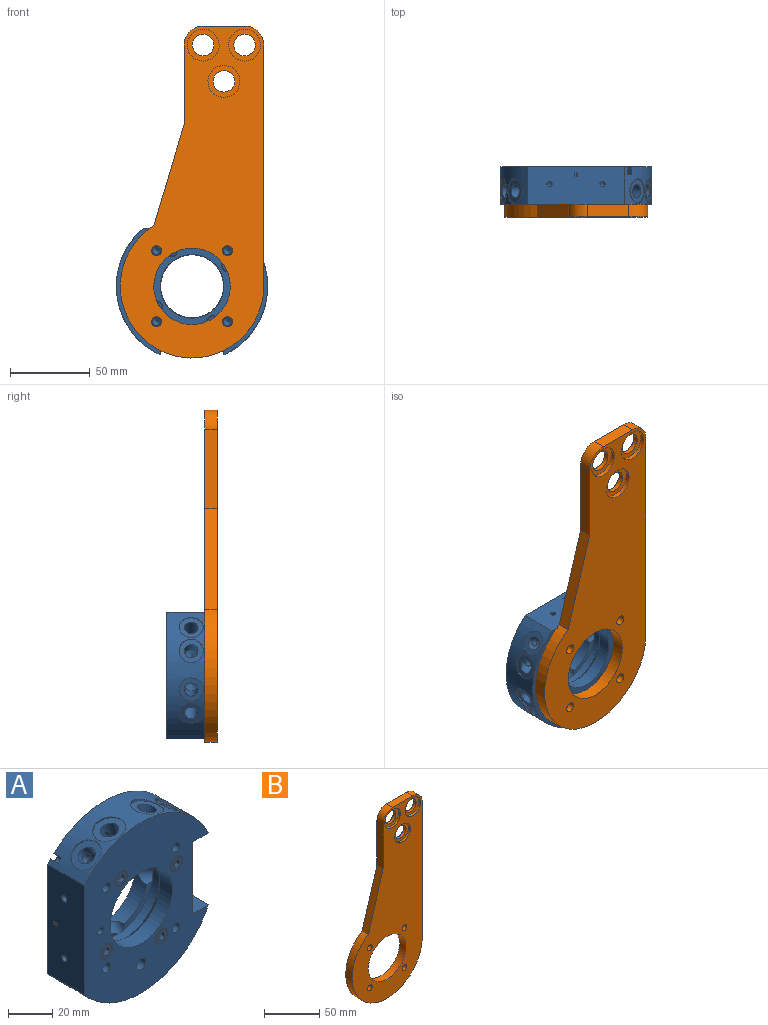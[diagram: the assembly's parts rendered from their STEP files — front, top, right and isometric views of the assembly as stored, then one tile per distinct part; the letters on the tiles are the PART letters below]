
ASSEMBLY  parts=2 mates=1
PART A: 247 faces, bbox 80.7x25x96.8 mm
  f0: plane 0.1x0.04mm, normal (0,0,-1), area 0mm2, adj f207,f224,f225,f241
  f1: plane 0.1x0.04mm, normal (0,0,1), area 0mm2, adj f207,f226,f227,f241
  f2: plane 0.5x0.1mm, normal (0,-0.89,-0.45), area 0.1mm2, adj f3,f4,f99,f178
  f3: plane 0.5x0.1mm, normal (0,0.89,-0.45), area 0.1mm2, adj f2,f5,f99,f178
  f4: plane 0.5x0.21mm, normal (0,-0.59,-0.8), area 0.1mm2, adj f2,f6,f99,f178
  f5: plane 0.5x0.21mm, normal (0,0.59,-0.8), area 0.1mm2, adj f3,f9,f99,f178
  f6: plane 0.5x0.16mm, normal (0,-0.31,-0.95), area 0.1mm2, adj f4,f14,f99,f178
  f7: plane 0.5x0.11mm, normal (0,0,1), area 0.1mm2, adj f15,f16,f56,f99
  f8: plane 0.5x0.16mm, normal (0,0,1), area 0.1mm2, adj f17,f18,f59,f99
  f9: plane 0.5x0.16mm, normal (0,0.31,-0.95), area 0.1mm2, adj f5,f19,f99,f178
  f10: plane 4.62x4mm, normal (0,-1,0), area 13.9mm2, adj f20,f21,f22,f23,f24,f25
  f11: plane 4.62x4mm, normal (0,-1,0), area 13.9mm2, adj f26,f27,f28,f29,f30,f31
  f12: plane 4.62x4mm, normal (0,-1,0), area 13.9mm2, adj f32,f33,f34,f35,f36,f37
  f13: plane 4.62x4mm, normal (0,-1,0), area 13.9mm2, adj f38,f39,f40,f41,f42,f43
  f14: plane 0.5x0.21mm, normal (0,0,-1), area 0.1mm2, adj f6,f44,f99,f178
  f15: plane 0.5x0.16mm, normal (0,-0.31,0.95), area 0.1mm2, adj f7,f45,f56,f99
  f16: plane 0.5x0.16mm, normal (0,0.31,0.95), area 0.1mm2, adj f7,f46,f56,f99
  f17: plane 0.5x0.16mm, normal (0,-0.31,0.95), area 0.1mm2, adj f8,f47,f59,f99
  f18: plane 0.5x0.16mm, normal (0,0.31,0.95), area 0.1mm2, adj f8,f48,f59,f99
  f19: plane 0.5x0.27mm, normal (0,0,-1), area 0.1mm2, adj f9,f49,f99,f178
  f20: plane 2x2mm, normal (0.5,0,-0.87), area 4.6mm2, adj f10,f21,f25,f50
  f21: plane 2x2mm, normal (-0.5,0,-0.87), area 4.6mm2, adj f10,f20,f22,f50
  f22: plane 2.31x2mm, normal (-1,0,0), area 4.6mm2, adj f10,f21,f23,f50
  f23: plane 2x2mm, normal (-0.5,0,0.87), area 4.6mm2, adj f10,f22,f24,f50
  f24: plane 2x2mm, normal (0.5,0,0.87), area 4.6mm2, adj f10,f23,f25,f50
  f25: plane 2.31x2mm, normal (1,0,0), area 4.6mm2, adj f10,f20,f24,f50
  f26: plane 2x2mm, normal (0.5,0,-0.87), area 4.6mm2, adj f11,f27,f31,f51
  f27: plane 2x2mm, normal (-0.5,0,-0.87), area 4.6mm2, adj f11,f26,f28,f51
  f28: plane 2.31x2mm, normal (-1,0,0), area 4.6mm2, adj f11,f27,f29,f51
  f29: plane 2x2mm, normal (-0.5,0,0.87), area 4.6mm2, adj f11,f28,f30,f51
  f30: plane 2x2mm, normal (0.5,0,0.87), area 4.6mm2, adj f11,f29,f31,f51
  f31: plane 2.31x2mm, normal (1,0,0), area 4.6mm2, adj f11,f26,f30,f51
  f32: plane 2x2mm, normal (0.5,0,-0.87), area 4.6mm2, adj f12,f33,f37,f52
  f33: plane 2x2mm, normal (-0.5,0,-0.87), area 4.6mm2, adj f12,f32,f34,f52
  f34: plane 2.31x2mm, normal (-1,0,0), area 4.6mm2, adj f12,f33,f35,f52
  f35: plane 2x2mm, normal (-0.5,0,0.87), area 4.6mm2, adj f12,f34,f36,f52
  f36: plane 2x2mm, normal (0.5,0,0.87), area 4.6mm2, adj f12,f35,f37,f52
  f37: plane 2.31x2mm, normal (1,0,0), area 4.6mm2, adj f12,f32,f36,f52
  f38: plane 2x2mm, normal (0.5,0,-0.87), area 4.6mm2, adj f13,f39,f43,f53
  f39: plane 2x2mm, normal (-0.5,0,-0.87), area 4.6mm2, adj f13,f38,f40,f53
  f40: plane 2.31x2mm, normal (-1,0,0), area 4.6mm2, adj f13,f39,f41,f53
  f41: plane 2x2mm, normal (-0.5,0,0.87), area 4.6mm2, adj f13,f40,f42,f53
  f42: plane 2x2mm, normal (0.5,0,0.87), area 4.6mm2, adj f13,f41,f43,f53
  f43: plane 2.31x2mm, normal (1,0,0), area 4.6mm2, adj f13,f38,f42,f53
  f44: plane 0.5x0.16mm, normal (0,0.31,-0.95), area 0.1mm2, adj f14,f54,f99,f178
  f45: plane 0.5x0.11mm, normal (0,-0.7,0.71), area 0.1mm2, adj f15,f55,f56,f99
  f46: plane 0.5x0.11mm, normal (0,0.7,0.71), area 0.1mm2, adj f16,f56,f57,f99
  f47: plane 0.5x0.11mm, normal (0,-0.7,0.71), area 0.1mm2, adj f17,f58,f59,f99
  f48: plane 0.5x0.11mm, normal (0,0.7,0.71), area 0.1mm2, adj f18,f59,f60,f99
  f49: plane 0.5x0.16mm, normal (0,-0.31,-0.95), area 0.1mm2, adj f19,f61,f99,f178
  f50: plane 7x7mm, normal (0,-1,0), area 24.6mm2, adj f20,f21,f22,f23,f24,f25,f63
  f51: plane 7x7mm, normal (0,-1,0), area 24.6mm2, adj f26,f27,f28,f29,f30,f31,f64
  f52: plane 7x7mm, normal (0,-1,0), area 24.6mm2, adj f32,f33,f34,f35,f36,f37,f65
  f53: plane 7x7mm, normal (0,-1,0), area 24.6mm2, adj f38,f39,f40,f41,f42,f43,f66
  f54: plane 0.5x0.21mm, normal (0,0.59,-0.8), area 0.1mm2, adj f44,f67,f99,f178
  f55: plane 0.5x0.16mm, normal (0,-0.95,0.32), area 0.1mm2, adj f45,f56,f68,f99
  f56: plane 1.3x0.74mm, normal (-1,0,0), area 0.9mm2, adj f7,f15,f16,f45,f46,f55,f57,f68
  f57: plane 0.5x0.16mm, normal (0,0.95,0.32), area 0.1mm2, adj f46,f56,f70,f99
  f58: plane 0.5x0.16mm, normal (0,-0.94,0.33), area 0.1mm2, adj f47,f59,f71,f99
  f59: plane 1.3x0.8mm, normal (-1,0,0), area 1mm2, adj f8,f17,f18,f47,f48,f58,f60,f71
  f60: plane 0.5x0.16mm, normal (0,0.95,0.32), area 0.1mm2, adj f48,f59,f73,f99
  f61: plane 0.5x0.21mm, normal (0,-0.59,-0.8), area 0.1mm2, adj f49,f74,f99,f178
  f62: plane 1.44x0.94mm, normal (1,0,0), area 0.7mm2, adj f75,f76,f77
  f63: cylinder r=3.5mm len=7mm, axis (0,1,0), area 127.5mm2, adj f50,f84
  f64: cylinder r=3.5mm len=7mm, axis (0,1,0), area 127.5mm2, adj f51,f85
  f65: cylinder r=3.5mm len=7mm, axis (0,1,0), area 127.5mm2, adj f52,f86
  f66: cylinder r=3.5mm len=7mm, axis (0,1,0), area 127.5mm2, adj f53,f87
  f67: plane 0.5x0.21mm, normal (0,0.79,-0.61), area 0.1mm2, adj f54,f98,f99,f178
  f68: plane 0.99x0.5mm, normal (0,-1,0), area 0.5mm2, adj f55,f56,f69,f99
  f69: plane 0.74x0.5mm, normal (0,0,-1), area 0.4mm2, adj f56,f68,f70,f99
  f70: plane 0.99x0.5mm, normal (0,1,0), area 0.5mm2, adj f56,f57,f69,f99
  f71: plane 0.99x0.5mm, normal (0,-1,0), area 0.5mm2, adj f58,f59,f72,f99
  f72: plane 0.8x0.5mm, normal (0,0,-1), area 0.4mm2, adj f59,f71,f73,f99
  f73: plane 0.99x0.5mm, normal (0,1,0), area 0.5mm2, adj f59,f60,f72,f99
  f74: plane 0.5x0.21mm, normal (0,-0.79,-0.61), area 0.1mm2, adj f61,f99,f100,f178
  f75: plane 1.44x0.5mm, normal (0,0.31,0.95), area 0.8mm2, adj f62,f76,f77,f105
  f76: plane 1.44x0.5mm, normal (0,0.31,-0.95), area 0.8mm2, adj f62,f75,f77,f105
  f77: plane 0.94x0.5mm, normal (0,-1,0), area 0.5mm2, adj f62,f75,f76,f105
  f78: cone r=0mm half-angle=59deg, axis (0,-1,0), area 22.2mm2, adj f112
  f79: cone r=0mm half-angle=59deg, axis (0,-1,0), area 22.2mm2, adj f113
  f80: cone r=0mm half-angle=59deg, axis (0,-1,0), area 22.2mm2, adj f114
  f81: cone r=0mm half-angle=59deg, axis (0,-1,0), area 22.2mm2, adj f115
  f82: plane 4x4mm, normal (0,-1,0), area 12.6mm2, adj f116
  f83: cone r=0mm half-angle=60deg, axis (0,-1,0), area 32.6mm2, adj f117
  f84: plane 8x8mm, normal (0,-1,0), area 11.8mm2, adj f63,f118
  f85: plane 8x8mm, normal (0,-1,0), area 11.8mm2, adj f64,f119
  f86: plane 8x8mm, normal (0,-1,0), area 11.8mm2, adj f65,f120
  f87: plane 8x8mm, normal (0,-1,0), area 11.8mm2, adj f66,f121
  f88: cone r=0mm half-angle=60deg, axis (-0.57,0,-0.82), area 66.5mm2, adj f124
  f89: cone r=0mm half-angle=60deg, axis (0.57,0,-0.82), area 66.5mm2, adj f125
  f90: cone r=0mm half-angle=60deg, axis (0.26,0,-0.97), area 66.5mm2, adj f126
  f91: cone r=0mm half-angle=60deg, axis (-0.26,0,-0.97), area 66.5mm2, adj f127
  f92: cone r=0mm half-angle=60deg, axis (0.57,0,0.82), area 66.5mm2, adj f128
  f93: cone r=0mm half-angle=60deg, axis (-0.57,0,0.82), area 66.5mm2, adj f129
  f94: cone r=0mm half-angle=60deg, axis (-0.26,0,0.97), area 66.5mm2, adj f130
  f95: cone r=0mm half-angle=60deg, axis (0.26,0,0.97), area 66.5mm2, adj f131
  f96: cone r=0mm half-angle=59deg, axis (-1,0,0), area 9.6mm2, adj f137
  f97: cone r=0mm half-angle=59deg, axis (-1,0,0), area 9.6mm2, adj f138
  f98: plane 0.5x0.26mm, normal (0,0.98,-0.2), area 0.1mm2, adj f67,f99,f139,f178
  f99: plane 2.5x1.93mm, normal (-1,0,0), area 2.6mm2, adj f2,f3,f4,f5,f6,f7,f8,f9
  f100: plane 0.5x0.26mm, normal (0,-0.98,-0.2), area 0.1mm2, adj f74,f99,f141,f178
  f101: plane 15.24x14.72mm, normal (0.26,0,0.97), area 124.8mm2, adj f131,f144
  f102: plane 15.24x14.72mm, normal (-0.26,0,0.97), area 124.8mm2, adj f130,f145
  f103: plane 15.24x12.48mm, normal (0.57,0,0.82), area 124.8mm2, adj f128,f146
  f104: plane 15.24x12.48mm, normal (-0.57,0,0.82), area 124.8mm2, adj f129,f147
  f105: plane 2.5x2.08mm, normal (1,0,0), area 1.7mm2, adj f75,f76,f77,f148,f149,f150,f151,f152
  f106: cone r=0mm half-angle=60deg, axis (1,0,0), area 5.5mm2, adj f156
  f107: cone r=0mm half-angle=60deg, axis (1,0,0), area 5.5mm2, adj f157
  f108: cone r=0mm half-angle=60deg, axis (1,0,0), area 5.5mm2, adj f158
  f109: cone r=0mm half-angle=60deg, axis (1,0,0), area 5.5mm2, adj f159
  f110: plane 15.24x14.72mm, normal (0.26,0,-0.97), area 124.8mm2, adj f126,f160
  f111: plane 15.24x12.48mm, normal (0.57,0,-0.82), area 124.8mm2, adj f125,f161
  f112: cylinder r=2.46mm len=13.83mm, axis (0,-1,0), area 213.6mm2, adj f78,f162
  f113: cylinder r=2.46mm len=13.83mm, axis (0,-1,0), area 213.6mm2, adj f79,f162
  f114: cylinder r=2.46mm len=13.83mm, axis (0,-1,0), area 213.6mm2, adj f80,f162
  f115: cylinder r=2.46mm len=13.83mm, axis (0,-1,0), area 213.6mm2, adj f81,f162
  f116: cylinder r=2mm len=13.85mm, axis (0,1,0), area 174mm2, adj f82,f162
  f117: cylinder r=3mm len=10mm, axis (0,-1,0), area 188.5mm2, adj f83,f162
  f118: cylinder r=4mm len=8mm, axis (0,1,0), area 145.8mm2, adj f84,f162
  f119: cylinder r=4mm len=8mm, axis (0,1,0), area 145.8mm2, adj f85,f162
  f120: cylinder r=4mm len=8mm, axis (0,1,0), area 145.8mm2, adj f86,f162
  f121: cylinder r=4mm len=8mm, axis (0,1,0), area 145.8mm2, adj f87,f162
  f122: plane 15.24x12.48mm, normal (-0.57,0,-0.82), area 124.8mm2, adj f124,f163
  f123: plane 15.24x14.72mm, normal (-0.26,0,-0.97), area 124.8mm2, adj f127,f164
  f124: cylinder r=4.28mm len=14.85mm, axis (0.57,0,0.82), area 306mm2, adj f88,f122,f165
  f125: cylinder r=4.28mm len=14.85mm, axis (-0.57,0,0.82), area 306mm2, adj f89,f111,f166
  f126: cylinder r=4.28mm len=13.94mm, axis (-0.26,0,0.97), area 306mm2, adj f90,f110,f167
  f127: cylinder r=4.28mm len=13.94mm, axis (0.26,0,0.97), area 306mm2, adj f91,f123,f168
  f128: cylinder r=4.28mm len=14.85mm, axis (0.57,0,0.82), area 306mm2, adj f92,f103,f169
  f129: cylinder r=4.28mm len=14.85mm, axis (-0.57,0,0.82), area 306mm2, adj f93,f104,f170
  f130: cylinder r=4.28mm len=13.94mm, axis (-0.26,0,0.97), area 306mm2, adj f94,f102,f171
  f131: cylinder r=4.28mm len=13.94mm, axis (0.26,0,0.97), area 306mm2, adj f95,f101,f172
  f132: plane 3.4x3.4mm, normal (0,1,0), area 9.1mm2, adj f173
  f133: plane 3.4x3.4mm, normal (0,1,0), area 9.1mm2, adj f174
  f134: plane 3.4x3.4mm, normal (0,1,0), area 9.1mm2, adj f175
  f135: plane 3.4x3.4mm, normal (0,1,0), area 9.1mm2, adj f176
  f136: cylinder r=20mm len=40mm, axis (0,1,0), area 1005.3mm2, adj f162,f177
  f137: cylinder r=1.62mm len=12.93mm, axis (1,0,0), area 131.7mm2, adj f96,f178
  f138: cylinder r=1.62mm len=12.93mm, axis (1,0,0), area 131.7mm2, adj f97,f178
  f139: plane 1.25x0.5mm, normal (0,1,0), area 0.6mm2, adj f98,f99,f140,f178
  f140: plane 2.5x0.5mm, normal (0,0,1), area 1.3mm2, adj f99,f139,f141,f178
  f141: plane 1.25x0.5mm, normal (0,-1,0), area 0.6mm2, adj f99,f100,f140,f178
  f142: plane 4.31x4.31mm, normal (0,1,0), area 11mm2, adj f182,f183,f184,f185
  f143: plane 4.31x4.31mm, normal (0,1,0), area 11mm2, adj f179,f180,f181,f185
  f144: cylinder r=7.62mm len=15.24mm, axis (0.26,0,0.97), area 33.2mm2, adj f101,f185
  f145: cylinder r=7.62mm len=15.24mm, axis (-0.26,0,0.97), area 33.2mm2, adj f102,f185
  f146: cylinder r=7.62mm len=15.24mm, axis (0.57,0,0.82), area 33.2mm2, adj f103,f185
  f147: cylinder r=7.62mm len=15.24mm, axis (-0.57,0,0.82), area 33.2mm2, adj f104,f185
  f148: plane 2.5x0.83mm, normal (0,-0.32,-0.95), area 1.3mm2, adj f105,f149,f155,f187
  f149: plane 0.5x0.42mm, normal (0,-1,0), area 0.2mm2, adj f105,f148,f150,f187
  f150: plane 2.5x0.83mm, normal (0,-0.32,0.95), area 1.3mm2, adj f105,f149,f151,f187
  f151: plane 0.5x0.31mm, normal (0,1,0), area 0.2mm2, adj f105,f150,f152,f187
  f152: plane 0.64x0.5mm, normal (0,0.31,-0.95), area 0.3mm2, adj f105,f151,f153,f187
  f153: plane 1.04x0.5mm, normal (0,1,0), area 0.5mm2, adj f105,f152,f154,f187
  f154: plane 0.64x0.5mm, normal (0,0.31,0.95), area 0.3mm2, adj f105,f153,f155,f187
  f155: plane 0.5x0.31mm, normal (0,1,0), area 0.2mm2, adj f105,f148,f154,f187
  f156: cylinder r=1.23mm len=6mm, axis (1,0,0), area 46.4mm2, adj f106,f187
  f157: cylinder r=1.23mm len=6mm, axis (1,0,0), area 46.4mm2, adj f107,f187
  f158: cylinder r=1.23mm len=6mm, axis (1,0,0), area 46.4mm2, adj f108,f187
  f159: cylinder r=1.23mm len=6mm, axis (1,0,0), area 46.4mm2, adj f109,f187
  f160: cylinder r=7.62mm len=15.24mm, axis (-0.26,0,0.97), area 33.2mm2, adj f110,f189
  f161: cylinder r=7.62mm len=15.24mm, axis (-0.57,0,0.82), area 33.2mm2, adj f111,f189
  f162: plane 95x79.58mm, normal (0,-1,0), area 4534.2mm2, adj f112,f113,f114,f115,f116,f117,f118,f119
  f163: cylinder r=7.62mm len=15.24mm, axis (0.57,0,0.82), area 33.2mm2, adj f122,f189
  f164: cylinder r=7.62mm len=15.24mm, axis (0.26,0,0.97), area 33.2mm2, adj f123,f189
  f165: cylinder r=2.5mm len=8.7mm, axis (0,-1,0), area 136.7mm2, adj f124,f190
  f166: cylinder r=2.5mm len=8.7mm, axis (0,-1,0), area 136.6mm2, adj f125,f191
  f167: cylinder r=2.5mm len=8.5mm, axis (0,-1,0), area 133.5mm2, adj f126,f192
  f168: cylinder r=2.5mm len=8.5mm, axis (0,-1,0), area 133.5mm2, adj f127,f193
  f169: cylinder r=2.5mm len=8.7mm, axis (0,-1,0), area 136.7mm2, adj f128,f194
  f170: cylinder r=2.5mm len=8.7mm, axis (0,-1,0), area 136.6mm2, adj f129,f195
  f171: cylinder r=2.5mm len=8.5mm, axis (0,-1,0), area 133.5mm2, adj f130,f196
  f172: cylinder r=2.5mm len=8.5mm, axis (0,-1,0), area 133.5mm2, adj f131,f197
  f173: cone r=0mm half-angle=45deg, axis (0,-1,0), area 4.9mm2, adj f132,f203
  f174: cone r=0mm half-angle=45deg, axis (0,-1,0), area 4.9mm2, adj f133,f204
  f175: cone r=0mm half-angle=45deg, axis (0,-1,0), area 4.9mm2, adj f134,f205
  f176: cone r=0mm half-angle=45deg, axis (0,-1,0), area 4.9mm2, adj f135,f206
  f177: cone r=0mm half-angle=45deg, axis (0,1,0), area 573.1mm2, adj f136,f208
  f178: plane 60.79x23.7mm, normal (-1,0,0), area 1419.8mm2, adj f2,f3,f4,f5,f6,f9,f14,f19
  f179: plane 5x1.75mm, normal (0.71,0,0.71), area 12.4mm2, adj f143,f180,f185,f209
  f180: cylinder r=1.5mm len=5mm, axis (0,1,0), area 23.6mm2, adj f143,f179,f181,f209
  f181: plane 5x1.75mm, normal (-0.71,0,-0.71), area 12.4mm2, adj f143,f180,f185,f209
  f182: plane 5x1.75mm, normal (0.71,0,-0.71), area 12.4mm2, adj f142,f183,f185,f209
  f183: cylinder r=1.5mm len=5mm, axis (0,1,0), area 23.6mm2, adj f142,f182,f184,f209
  f184: plane 5x1.75mm, normal (-0.71,0,0.71), area 12.4mm2, adj f142,f183,f185,f209
  f185: cylinder r=47.5mm len=79.58mm, axis (0,-1,0), area 1503.6mm2, adj f142,f143,f144,f145,f146,f147,f162,f178
  f186: plane 23.7x10.08mm, normal (0,0,-1), area 239mm2, adj f162,f185,f187,f209
  f187: plane 40x23.7mm, normal (1,0,0), area 926.7mm2, adj f148,f149,f150,f151,f152,f153,f154,f155
  f188: plane 23.7x10.08mm, normal (0,0,1), area 239mm2, adj f162,f187,f189,f209
  f189: cylinder r=47.5mm len=79.58mm, axis (0,-1,0), area 1533.6mm2, adj f160,f161,f162,f163,f164,f178,f188,f209
  f190: cone r=0mm half-angle=45deg, axis (0,1,0), area 84mm2, adj f165,f209
  f191: cone r=0mm half-angle=45deg, axis (0,1,0), area 84mm2, adj f166,f209
  f192: cone r=0mm half-angle=45deg, axis (0,1,0), area 84mm2, adj f167,f209
  f193: cone r=0mm half-angle=45deg, axis (0,1,0), area 84mm2, adj f168,f209
  f194: cone r=0mm half-angle=45deg, axis (0,1,0), area 84mm2, adj f169,f209
  f195: cone r=0mm half-angle=45deg, axis (0,1,0), area 84mm2, adj f170,f209
  f196: cone r=0mm half-angle=45deg, axis (0,1,0), area 84mm2, adj f171,f209
  f197: cone r=0mm half-angle=45deg, axis (0,1,0), area 84mm2, adj f172,f209
  f198: plane 9.31x4.44mm, normal (0,1,0), area 17.4mm2, adj f208,f211
  f199: cylinder r=2mm len=3.82mm, axis (0,1,0), area 5mm2, adj f200,f215
  f200: plane 8.56x3.13mm, normal (0,1,0), area 12mm2, adj f199,f208,f215
  f201: cone r=0mm half-angle=60deg, axis (0,1,0), area 14.5mm2, adj f216
  f202: plane 9.31x4.44mm, normal (0,1,0), area 16.9mm2, adj f208,f213,f216
  f203: cylinder r=2mm len=17.8mm, axis (0,1,0), area 223.7mm2, adj f173,f218
  f204: cylinder r=2mm len=17.8mm, axis (0,1,0), area 223.7mm2, adj f174,f219
  f205: cylinder r=2mm len=17.8mm, axis (0,1,0), area 223.7mm2, adj f175,f220
  f206: cylinder r=2mm len=17.8mm, axis (0,1,0), area 223.7mm2, adj f176,f221
  f207: plane 7.14x0.8mm, normal (-1,0,0), area 5.7mm2, adj f0,f1,f225,f226,f229,f238,f242,f244
  f208: cylinder r=23mm len=46mm, axis (0,1,0), area 686.4mm2, adj f177,f198,f200,f202,f210,f212,f214,f222
  f209: plane 95x79.58mm, normal (0,1,0), area 2435.5mm2, adj f178,f179,f180,f181,f182,f183,f184,f185
  f210: plane 18.61x18.61mm, normal (0,-1,0), area 79.3mm2, adj f208,f211,f231,f239
  f211: cylinder r=4.75mm len=9.62mm, axis (0.71,-0.71,0), area 72.3mm2, adj f198,f210,f212,f231
  f212: plane 18.61x18.61mm, normal (0,-1,0), area 79.3mm2, adj f208,f211,f213,f231
  f213: cylinder r=4.75mm len=9.62mm, axis (0,0.71,-0.71), area 83.8mm2, adj f202,f212,f214,f216,f231
  f214: plane 18.61x18.61mm, normal (0,-1,0), area 79.3mm2, adj f208,f213,f215,f231
  f215: cylinder r=4.75mm len=9.5mm, axis (0.71,0.71,0), area 69.5mm2, adj f199,f200,f214,f222,f231
  f216: cylinder r=2mm len=11.1mm, axis (0,1,0), area 139.5mm2, adj f201,f202,f213,f232
  f217: plane 4x4mm, normal (0,1,0), area 12.6mm2, adj f233
  f218: plane 4.5x4.5mm, normal (0,1,0), area 3.3mm2, adj f203,f234
  f219: plane 4.5x4.5mm, normal (0,1,0), area 3.3mm2, adj f204,f235
  f220: plane 4.5x4.5mm, normal (0,1,0), area 3.3mm2, adj f205,f236
  f221: plane 4.5x4.5mm, normal (0,1,0), area 3.3mm2, adj f206,f237
  f222: plane 18.61x18.61mm, normal (0,-1,0), area 79.3mm2, adj f208,f215,f231,f239
  f223: cone r=0mm half-angle=60deg, axis (0,1,0), area 14.5mm2, adj f241
  f224: plane 0.38x0.13mm, normal (0,1,0), area 0mm2, adj f0,f239,f241,f244
  f225: plane 0.4x0.04mm, normal (0,1,0), area 0mm2, adj f0,f207,f241
  f226: plane 0.4x0.04mm, normal (0,1,0), area 0mm2, adj f1,f207,f241
  f227: plane 4x2.19mm, normal (0,1,0), area 1.5mm2, adj f1,f229,f241
  f228: plane 8.21x2.78mm, normal (0,1,0), area 12mm2, adj f208,f239,f241
  f229: cylinder r=2mm len=6.9mm, axis (0,1,0), area 44.5mm2, adj f207,f227,f241,f242
  f230: cylinder r=31mm len=62mm, axis (0,-1,0), area 19.5mm2, adj f209,f243
  f231: cylinder r=19.75mm len=39.5mm, axis (0,-1,0), area 808.5mm2, adj f210,f211,f212,f213,f214,f215,f222,f239
  f232: torus R=3.1mm, axis (0,1,0), area 17.5mm2, adj f216,f243
  f233: cylinder r=2mm len=4mm, axis (0,1,0), area 0.6mm2, adj f217,f243
  f234: cylinder r=2.25mm len=18mm, axis (0,1,0), area 254.5mm2, adj f218,f243
  f235: cylinder r=2.25mm len=18mm, axis (0,1,0), area 254.5mm2, adj f219,f243
  f236: cylinder r=2.25mm len=18mm, axis (0,1,0), area 254.5mm2, adj f220,f243
  f237: cylinder r=2.25mm len=18mm, axis (0,1,0), area 254.5mm2, adj f221,f243
  f238: torus R=3.1mm, axis (0,1,0), area 0.4mm2, adj f207,f242,f243,f246
  f239: cylinder r=4.75mm len=9.5mm, axis (0,-0.71,-0.71), area 75.9mm2, adj f210,f222,f224,f228,f231,f240,f241,f244
  f240: plane 0.59x0.13mm, normal (0,1,0), area 0mm2, adj f239,f241,f244
  f241: cylinder r=2mm len=11.1mm, axis (0,1,0), area 54.6mm2, adj f0,f1,f223,f224,f225,f226,f227,f228
  f242: torus R=3.1mm, axis (0,1,0), area 9.2mm2, adj f207,f229,f238,f243,f245
  f243: plane 62x62mm, normal (0,1,0), area 1669.7mm2, adj f230,f231,f232,f233,f234,f235,f236,f237
  f244: cylinder r=2mm len=6.9mm, axis (0,1,0), area 37mm2, adj f207,f224,f239,f240,f241,f246
  f245: torus R=3.1mm, axis (0,1,0), area 0.5mm2, adj f241,f242,f243,f246
  f246: torus R=3.1mm, axis (0,1,0), area 9.2mm2, adj f207,f238,f243,f244,f245
PART B: 29 faces, bbox 90x8x208.4 mm
  f0: cylinder r=6.75mm len=13.5mm, axis (0,1,0), area 127.2mm2, adj f19,f26
  f1: cylinder r=6.75mm len=13.5mm, axis (0,1,0), area 127.2mm2, adj f21,f28
  f2: cylinder r=6.75mm len=13.5mm, axis (0,1,0), area 127.2mm2, adj f17,f24
  f3: plane 151.4x8mm, normal (1,0,0), area 1211.2mm2, adj f4,f14,f15,f16
  f4: cylinder r=12mm len=12mm, axis (0,1,0), area 150.8mm2, adj f3,f5,f15,f16
  f5: plane 26x8mm, normal (0,0,1), area 208mm2, adj f4,f6,f15,f16
  f6: cylinder r=12mm len=12mm, axis (0,1,0), area 150.8mm2, adj f5,f7,f15,f16
  f7: plane 50x8mm, normal (-1,0,0), area 400mm2, adj f6,f8,f15,f16
  f8: plane 63.33x19mm, normal (-0.96,0,0.29), area 529mm2, adj f7,f14,f15,f16
  f9: cylinder r=3.1mm len=8mm, axis (0,1,0), area 155.8mm2, adj f15,f16
  f10: cylinder r=3.1mm len=8mm, axis (0,1,0), area 155.8mm2, adj f15,f16
  f11: cylinder r=24mm len=48mm, axis (0,1,0), area 1206.4mm2, adj f15,f16
  f12: cylinder r=3.1mm len=8mm, axis (0,1,0), area 155.8mm2, adj f15,f16
  f13: cylinder r=3.1mm len=8mm, axis (0,1,0), area 155.8mm2, adj f15,f16
  f14: cylinder r=45mm len=90mm, axis (0,1,0), area 1493.9mm2, adj f3,f8,f15,f16
  f15: plane 208.4x90mm, normal (0,-1,0), area 10305.2mm2, adj f3,f4,f5,f6,f7,f8,f9,f10
  f16: plane 208.4x90mm, normal (0,1,0), area 10305.3mm2, adj f3,f4,f5,f6,f7,f8,f9,f10
  f17: plane 20x20mm, normal (0,-1,0), area 171.1mm2, adj f2,f18
  f18: cylinder r=10mm len=20mm, axis (0,-1,0), area 157.1mm2, adj f15,f17
  f19: plane 20x20mm, normal (0,-1,0), area 171mm2, adj f0,f20
  f20: cylinder r=10mm len=20mm, axis (0,-1,0), area 157.1mm2, adj f15,f19
  f21: plane 20x20mm, normal (0,-1,0), area 171mm2, adj f1,f22
  f22: cylinder r=10mm len=20mm, axis (0,-1,0), area 157.1mm2, adj f15,f21
  f23: cylinder r=10mm len=20mm, axis (0,1,0), area 157.1mm2, adj f16,f24
  f24: plane 20x20mm, normal (0,1,0), area 171mm2, adj f2,f23
  f25: cylinder r=10mm len=20mm, axis (0,1,0), area 157.1mm2, adj f16,f26
  f26: plane 20x20mm, normal (0,1,0), area 171mm2, adj f0,f25
  f27: cylinder r=10mm len=20mm, axis (0,1,0), area 157.1mm2, adj f16,f28
  f28: plane 20x20mm, normal (0,1,0), area 171mm2, adj f1,f27
PLACE A rot(axis=(0,1,0),90deg) t=(-56.89,-25.79,-54.63)mm
PLACE B t=(-56.89,-25.79,4.57)mm
MATE cylindrical A.f136 <-> B.f11  axis (0,-1,0) through (-56.89,-25.79,-54.63)mm
